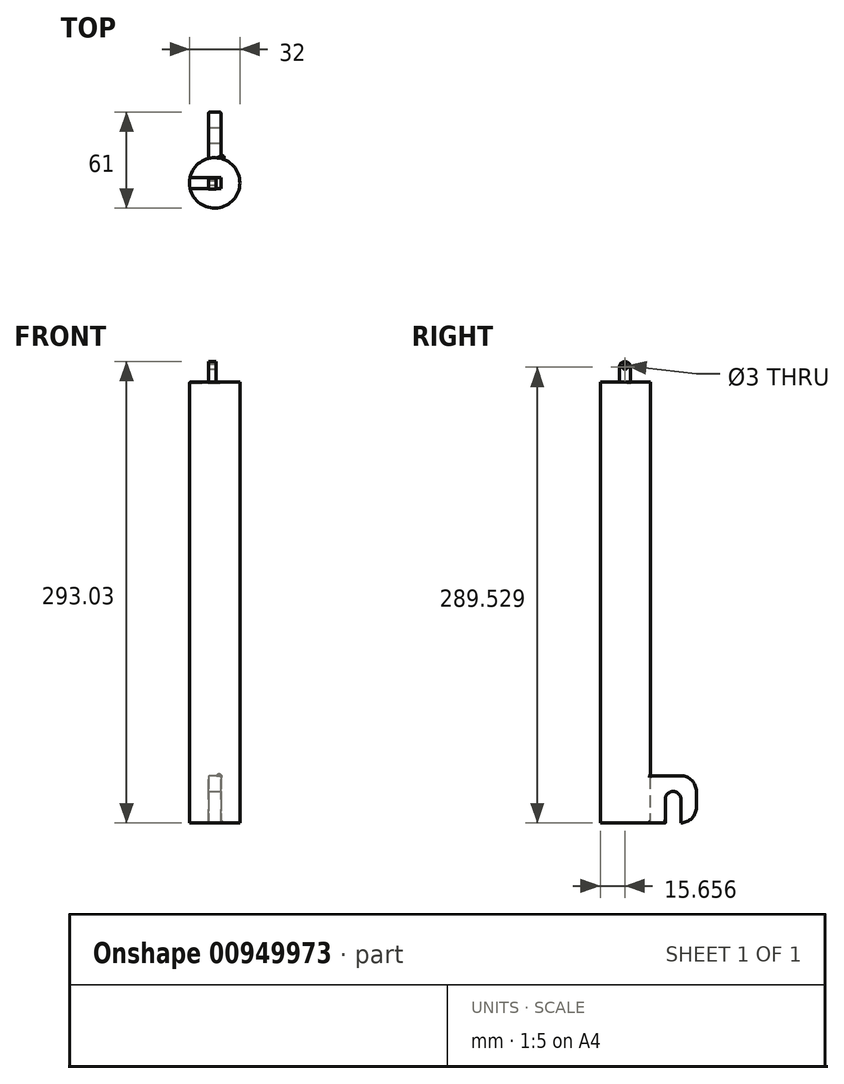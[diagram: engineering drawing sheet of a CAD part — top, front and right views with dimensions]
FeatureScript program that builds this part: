
annotation { "Feature Type Name" : "Feature", "Feature Type Description" : "" }
export const myFeature = defineFeature(function(context is Context, id is Id, definition is map)
    precondition{}
    {
        {
            var Q0;
            Q0=qCreatedBy(makeId("Top.planeOp"),FACE);
            var sketch = newSketch(context, id + "F0", { "sketchPlane" : qUnion([Q0])});
            skCircle(sketch, "E0", {"center": v(0, 0) * mm, "radius": 16 * mm});
            skSolve(sketch);
        }
        {
            var Q0;
            Q0 = qSketchRegion(id + "F0", true);
            extrude(context, id + "F1", {"entities" : qUnion([Q0]), "depth" : 280 * mm, "offsetDistance" : 25 * mm});
        }
        {
            var Q0;
            Q0=qCreatedBy(makeId("Right.planeOp"),FACE);
            var sketch = newSketch(context, id + "F2", { "sketchPlane" : qUnion([Q0])});
            skLineSegment(sketch, "E1.bottom", {"start": v(0, 30) * mm, "end": v(45, 30) * mm});
            skLineSegment(sketch, "E1.top", {"start": v(0, 0) * mm, "end": v(45, 0) * mm});
            skLineSegment(sketch, "E1.left", {"start": v(0, 30) * mm, "end": v(0, 0) * mm});
            skLineSegment(sketch, "E1.right", {"start": v(45, 30) * mm, "end": v(45, 0) * mm});
            skSolve(sketch);
        }
        {
            var Q0;
            Q0 = qSketchRegion(id + "F2", true);
            extrude(context, id + "F3", {"entities" : qUnion([Q0]), "operationType" : NewBodyOperationType.ADD, "depth" : 8 * mm, "offsetDistance" : 25 * mm, "symmetric" : true});
        }
        {
            var Q0;
            Q0=makeQuery(id+"F3.opExtrude","CAP_FACE",FACE,{"disambiguationData":[OSD([sQuery(id+"F2.wireOp",EDGE,"E1.bottom"),sQuery(id+"F2.wireOp",EDGE,"E1.top"),sQuery(id+"F2.wireOp",EDGE,"E1.left"),sQuery(id+"F2.wireOp",EDGE,"E1.right")])],"isStart":false});
            var sketch = newSketch(context, id + "F4", { "sketchPlane" : qUnion([Q0])});
            skCircle(sketch, "E2", {"center": v(30.25, 15) * mm, "radius": 5 * mm});
            skLineSegment(sketch, "E3", {"start": v(35.25, 15) * mm, "end": v(35.25, 0) * mm});
            skLineSegment(sketch, "E4", {"start": v(25.25, 15) * mm, "end": v(25.25, 0) * mm});
            skLineSegment(sketch, "E5", {"start": v(45, 15) * mm, "end": v(15.5, 15) * mm, "construction": true});
            skCircle(sketch, "E6", {"center": v(0, 286.56) * mm, "radius": 3.5 * mm});
            skCircle(sketch, "E7", {"center": v(0, 286.56) * mm, "radius": 1.5 * mm});
            skLineSegment(sketch, "E8", {"start": v(3.5, 286.56) * mm, "end": v(3.5, 279.52) * mm});
            skLineSegment(sketch, "E9", {"start": v(-3.5, 286.56) * mm, "end": v(-3.5, 279.67) * mm});
            skLineSegment(sketch, "E10", {"start": v(-3.5, 279.67) * mm, "end": v(3.5, 279.52) * mm});
            skSolve(sketch);
        }
        {
            var Q0;
            Q0 = qSketchRegion(id + "F4", true);
            var Q1;
            {var subQ0=sQuery(id+"F4.wireOp",EDGE,"E3");Q1=makeQuery(id+"F4.imprint","IMPRINT",FACE,{"disambiguationData":[TD([[makeQuery(id+"F4.imprint","IMPRINT",EDGE,{"derivedFrom":subQ0}),-1.0]])]});}
            extrude(context, id + "F5", {"entities" : qUnion([Q0, Q1]), "operationType" : NewBodyOperationType.REMOVE, "oppositeDirection" : true, "depth" : 25 * mm, "offsetDistance" : 25 * mm});
        }
        {
            var Q0;
            Q0=makeQuery(id+"F3.opExtrude","SWEPT_EDGE",EDGE,{"disambiguationData":[OSD([sQuery(id+"F2.wireOp",EDGE,"E1.bottom"),sQuery(id+"F2.wireOp",EDGE,"E1.right")])]});
            var Q1;
            Q1=makeQuery(id+"F3.opExtrude","SWEPT_EDGE",EDGE,{"disambiguationData":[OSD([sQuery(id+"F2.wireOp",EDGE,"E1.top"),sQuery(id+"F2.wireOp",EDGE,"E1.right")])]});
            fillet(context, id + "F6", {"entities" : qUnion([Q0, Q1]), "tangentPropagation" : true, "radius" : 10 * mm, "defaultsChanged" : true, "vertexSettings" : [], "allowEdgeOverflow" : false});
        }
        {
            var Q0;
            {var subQ0=sQuery(id+"F2.wireOp",EDGE,"E1.right");var subQ1=sQuery(id+"F2.wireOp",EDGE,"E1.bottom");Q0=makeQuery(id+"F6.opFillet","BLEND_EDGE",EDGE,{"blendedFrom":[makeQuery(id+"F3.opExtrude","SWEPT_EDGE",EDGE,{"disambiguationData":[OSD([subQ1,subQ0])]}),makeQuery(id+"F3.opExtrude","CAP_FACE",FACE,{"disambiguationData":[OSD([subQ1,sQuery(id+"F2.wireOp",EDGE,"E1.top"),sQuery(id+"F2.wireOp",EDGE,"E1.left"),subQ0])],"isStart":false})],"blendedInto":[makeQuery(id+"F3.opExtrude","CAP_FACE",FACE,{"disambiguationData":[OSD([subQ1,sQuery(id+"F2.wireOp",EDGE,"E1.top"),sQuery(id+"F2.wireOp",EDGE,"E1.left"),subQ0])],"isStart":false})]});}
            var Q1;
            Q1=makeQuery(id+"F3.opExtrude","CAP_EDGE",EDGE,{"disambiguationData":[OSD([sQuery(id+"F2.wireOp",EDGE,"E1.right")])],"isStart":true});
            var Q2;
            Q2=makeQuery(id+"F3.opExtrude","CAP_FACE",FACE,{"disambiguationData":[OSD([sQuery(id+"F2.wireOp",EDGE,"E1.bottom"),sQuery(id+"F2.wireOp",EDGE,"E1.top"),sQuery(id+"F2.wireOp",EDGE,"E1.left"),sQuery(id+"F2.wireOp",EDGE,"E1.right")])],"isStart":false});
            fillet(context, id + "F7", {"entities" : qUnion([Q0, Q1, Q2]), "tangentPropagation" : true, "radius" : 1 * mm, "defaultsChanged" : false, "vertexSettings" : [], "allowEdgeOverflow" : false});
        }
        {
            var Q0;
            Q0=makeQuery(id+"F3.opExtrude","CAP_FACE",FACE,{"disambiguationData":[OSD([sQuery(id+"F2.wireOp",EDGE,"E1.bottom"),sQuery(id+"F2.wireOp",EDGE,"E1.top"),sQuery(id+"F2.wireOp",EDGE,"E1.left"),sQuery(id+"F2.wireOp",EDGE,"E1.right")])],"isStart":true});
            var sketch = newSketch(context, id + "F8", { "sketchPlane" : qUnion([Q0])});
            skLineSegment(sketch, "E11.bottom", {"start": v(-3.16, 279.53) * mm, "end": v(3.84, 279.53) * mm});
            skLineSegment(sketch, "E11.top", {"start": v(-3.16, 289.53) * mm, "end": v(3.84, 289.53) * mm});
            skLineSegment(sketch, "E11.left", {"start": v(-3.16, 279.53) * mm, "end": v(-3.16, 289.53) * mm});
            skLineSegment(sketch, "E11.right", {"start": v(3.84, 279.53) * mm, "end": v(3.84, 289.53) * mm});
            skCircle(sketch, "E12", {"center": v(0.34, 289.53) * mm, "radius": 3.5 * mm});
            skCircle(sketch, "E13", {"center": v(0.34, 289.53) * mm, "radius": 1.5 * mm});
            skSolve(sketch);
        }
        {
            var Q0;
            Q0 = qSketchRegion(id + "F8", true);
            extrude(context, id + "F9", {"entities" : qUnion([Q0]), "operationType" : NewBodyOperationType.ADD, "oppositeDirection" : true, "depth" : 5 * mm, "offsetDistance" : 25 * mm});
        }
    });
